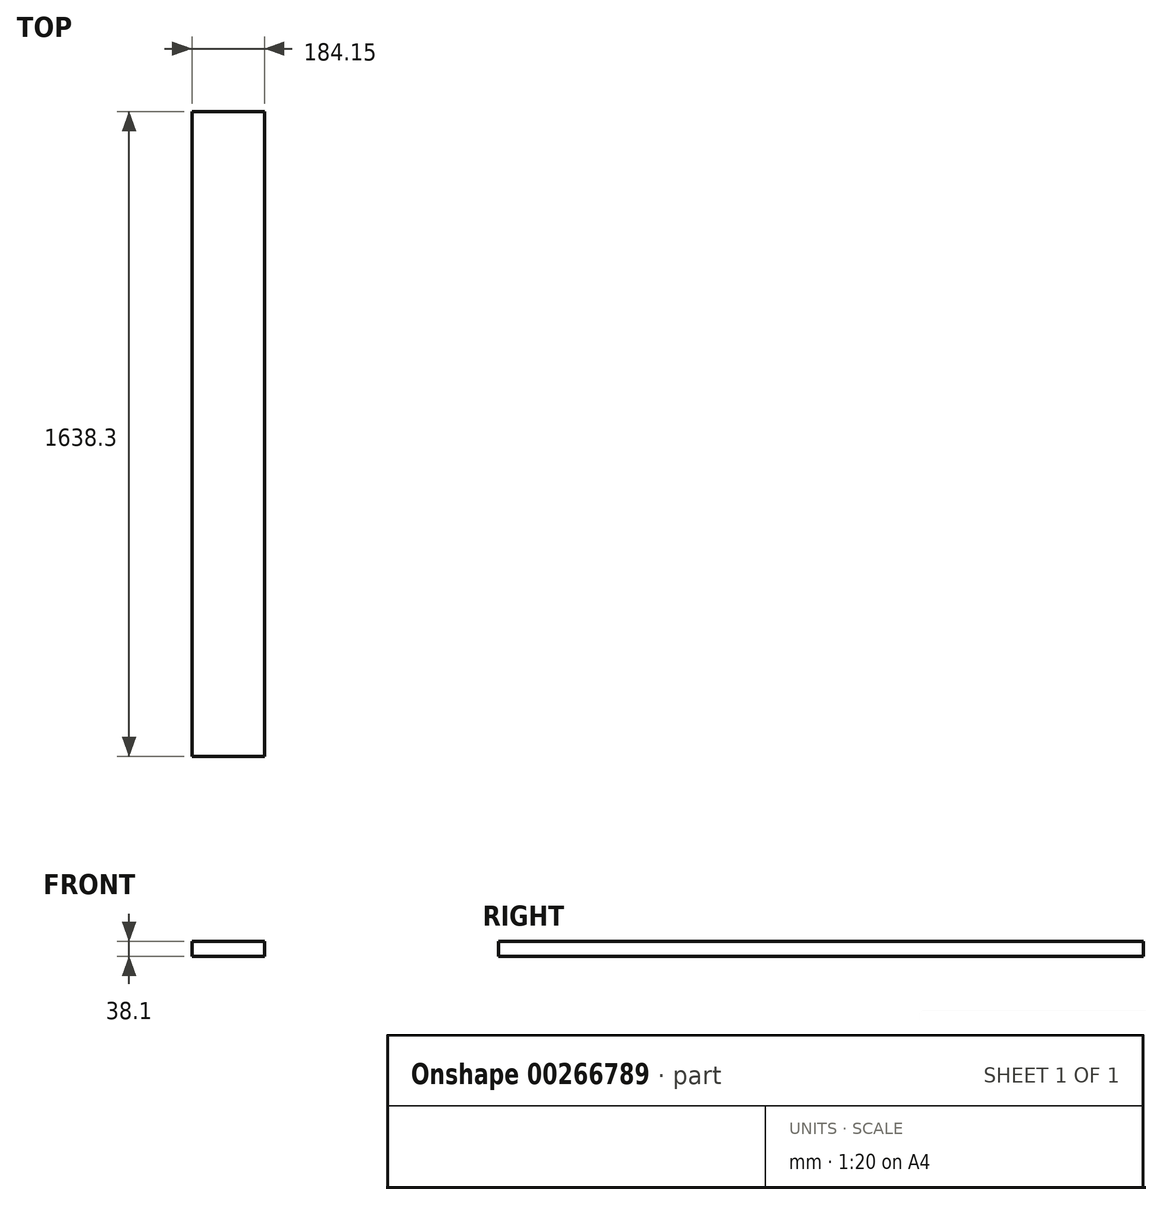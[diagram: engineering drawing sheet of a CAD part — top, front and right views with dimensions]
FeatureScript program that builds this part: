
annotation { "Feature Type Name" : "Feature", "Feature Type Description" : "" }
export const myFeature = defineFeature(function(context is Context, id is Id, definition is map)
    precondition{}
    {
        {
            var Q0;
            Q0=qCreatedBy(makeId("Front.planeOp"),FACE);
            var sketch = newSketch(context, id + "F0", { "sketchPlane" : qUnion([Q0])});
            skLineSegment(sketch, "E0.bottom", {"start": v(-48.34, 23.68) * mm, "end": v(135.8, 23.68) * mm});
            skLineSegment(sketch, "E0.top", {"start": v(-48.34, -14.42) * mm, "end": v(135.8, -14.42) * mm});
            skLineSegment(sketch, "E0.left", {"start": v(-48.34, 23.68) * mm, "end": v(-48.34, -14.42) * mm});
            skLineSegment(sketch, "E0.right", {"start": v(135.8, 23.68) * mm, "end": v(135.8, -14.42) * mm});
            skSolve(sketch);
        }
        {
            var Q0;
            Q0=qSketchRegion(id+"F0",true);
            extrude(context, id + "F1", {"entities" : qUnion([Q0]), "depth" : 1638.3 * mm});
        }
    });
